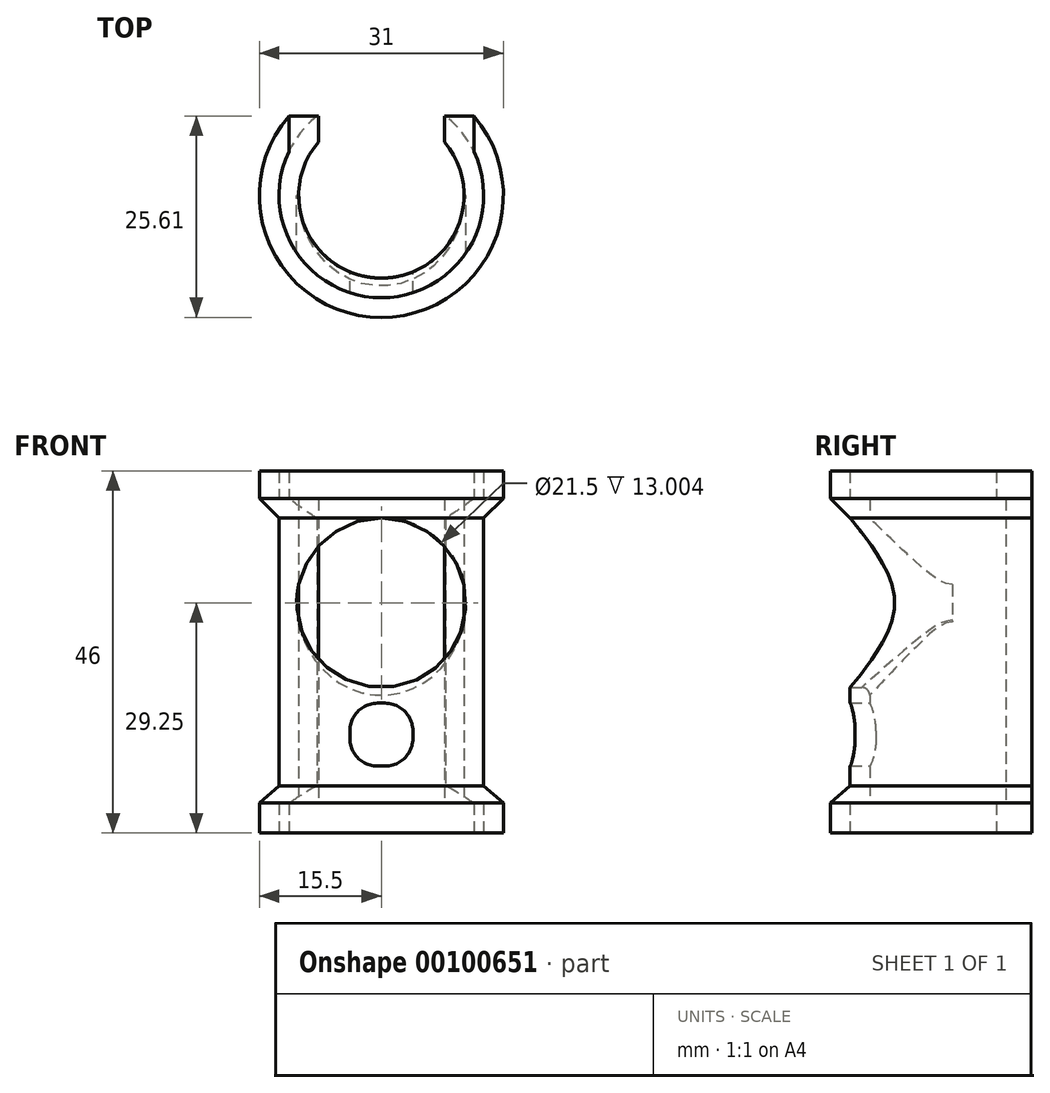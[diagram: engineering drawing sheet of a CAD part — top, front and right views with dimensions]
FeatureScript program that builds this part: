
annotation { "Feature Type Name" : "Feature", "Feature Type Description" : "" }
export const myFeature = defineFeature(function(context is Context, id is Id, definition is map)
    precondition{}
    {
        {
            var Q0;
            Q0=qCreatedBy(makeId("Front.planeOp"),FACE);
            var sketch = newSketch(context, id + "F0", { "sketchPlane" : qUnion([Q0])});
            skLineSegment(sketch, "E0", {"start": v(-13, 0) * mm, "end": v(-13, 3.8) * mm});
            skLineSegment(sketch, "E1", {"start": v(-13, 3.8) * mm, "end": v(-10.5, 3.8) * mm});
            skLineSegment(sketch, "E2", {"start": v(-10.5, 3.8) * mm, "end": v(-10.5, 42.5) * mm});
            skLineSegment(sketch, "E3", {"start": v(-13, 42.5) * mm, "end": v(-13, 46) * mm});
            skLineSegment(sketch, "E4", {"start": v(-13, 42.5) * mm, "end": v(-10.5, 42.5) * mm});
            skLineSegment(sketch, "E5", {"start": v(-13, 46) * mm, "end": v(-15.5, 46) * mm});
            skLineSegment(sketch, "E6", {"start": v(-15.5, 46) * mm, "end": v(-15.5, 42.5) * mm});
            skLineSegment(sketch, "E7", {"start": v(-13, 40) * mm, "end": v(-13, 6) * mm});
            skLineSegment(sketch, "E8", {"start": v(-15.5, 3.8) * mm, "end": v(-15.5, 0) * mm});
            skLineSegment(sketch, "E9", {"start": v(-15.5, 0) * mm, "end": v(-13, 0) * mm});
            skLineSegment(sketch, "E10", {"start": v(0, 0) * mm, "end": v(0, 49.8) * mm, "construction": true});
            skLineSegment(sketch, "E11", {"start": v(-15.5, 42.5) * mm, "end": v(-13, 40) * mm});
            skLineSegment(sketch, "E12", {"start": v(-15.5, 3.8) * mm, "end": v(-13, 6) * mm});
            skPoint(sketch, "E13.orphan", {"position": v(-13, 41) * mm});
            skPoint(sketch, "E14.orphan", {"position": v(-13, 3.5) * mm});
            skSolve(sketch);
        }
        {
            var Q0;
            Q0 = qSketchRegion(id + "F0", true);
            var Q1;
            Q1=sQuery(id+"F0.wireOp",EDGE,"E10");
            revolve(context, id + "F1", {"entities" : qUnion([Q0]), "axis" : qUnion([Q1]), "revolveType" : RevolveType.FULL});
        }
        {
            var Q0;
            Q0=makeQuery(id+"F1.opRevolve","SWEPT_FACE",FACE,{"disambiguationData":[OSD([sQuery(id+"F0.wireOp",EDGE,"E5")])]});
            var sketch = newSketch(context, id + "F2", { "sketchPlane" : qUnion([Q0])});
            skLineSegment(sketch, "E15.bottom", {"start": v(-8, 18.1) * mm, "end": v(8, 18.1) * mm});
            skLineSegment(sketch, "E15.top", {"start": v(-8, 5.31) * mm, "end": v(8, 5.31) * mm});
            skLineSegment(sketch, "E15.left", {"start": v(-8, 18.1) * mm, "end": v(-8, 5.31) * mm});
            skLineSegment(sketch, "E15.right", {"start": v(8, 18.1) * mm, "end": v(8, 5.31) * mm});
            skSolve(sketch);
        }
        {
            var Q0;
            Q0 = qSketchRegion(id + "F2", true);
            extrude(context, id + "F3", {"entities" : qUnion([Q0]), "operationType" : NewBodyOperationType.REMOVE, "endBound" : BoundingType.THROUGH_ALL, "oppositeDirection" : true, "depth" : 25 * mm});
        }
        {
            var Q0;
            Q0=makeQuery(id+"F1.opRevolve","SWEPT_FACE",FACE,{"disambiguationData":[OSD([sQuery(id+"F0.wireOp",EDGE,"E5")])]});
            var sketch = newSketch(context, id + "F4", { "sketchPlane" : qUnion([Q0])});
            skLineSegment(sketch, "E16.bottom", {"start": v(-11.75, 4.07) * mm, "end": v(11.75, 4.07) * mm});
            skLineSegment(sketch, "E16.top", {"start": v(-11.75, 17.53) * mm, "end": v(11.75, 17.53) * mm});
            skLineSegment(sketch, "E16.left", {"start": v(-11.75, 4.07) * mm, "end": v(-11.75, 17.53) * mm});
            skLineSegment(sketch, "E16.right", {"start": v(11.75, 4.07) * mm, "end": v(11.75, 17.53) * mm});
            skSolve(sketch);
        }
        {
            var Q0;
            Q0 = qSketchRegion(id + "F4", true);
            var Q1;
            Q1=makeQuery(id+"F1.opRevolve","SWEPT_FACE",FACE,{"disambiguationData":[OSD([sQuery(id+"F0.wireOp",EDGE,"E4")])]});
            extrude(context, id + "F5", {"entities" : qUnion([Q0]), "operationType" : NewBodyOperationType.REMOVE, "endBound" : BoundingType.UP_TO_SURFACE, "oppositeDirection" : true, "endBoundEntityFace" : qUnion([Q1]), "depth" : 25 * mm});
        }
        {
            var Q0;
            Q0=makeQuery(id+"F1.opRevolve","SWEPT_FACE",FACE,{"disambiguationData":[OSD([sQuery(id+"F0.wireOp",EDGE,"E9")])]});
            var sketch = newSketch(context, id + "F6", { "sketchPlane" : qUnion([Q0])});
            skLineSegment(sketch, "E17.bottom", {"start": v(-11.75, -15.87) * mm, "end": v(11.75, -15.87) * mm});
            skLineSegment(sketch, "E17.top", {"start": v(-11.75, -2.84) * mm, "end": v(11.75, -2.84) * mm});
            skLineSegment(sketch, "E17.left", {"start": v(-11.75, -15.87) * mm, "end": v(-11.75, -2.84) * mm});
            skLineSegment(sketch, "E17.right", {"start": v(11.75, -15.87) * mm, "end": v(11.75, -2.84) * mm});
            skSolve(sketch);
        }
        {
            var Q0;
            Q0 = qSketchRegion(id + "F6", true);
            var Q1;
            Q1=makeQuery(id+"F1.opRevolve","SWEPT_FACE",FACE,{"disambiguationData":[OSD([sQuery(id+"F0.wireOp",EDGE,"E1")])]});
            extrude(context, id + "F7", {"entities" : qUnion([Q0]), "operationType" : NewBodyOperationType.REMOVE, "endBound" : BoundingType.UP_TO_SURFACE, "oppositeDirection" : true, "endBoundEntityFace" : qUnion([Q1]), "depth" : 25 * mm});
        }
        {
            var Q0;
            Q0=qCreatedBy(makeId("Front.planeOp"),FACE);
            var sketch = newSketch(context, id + "F8", { "sketchPlane" : qUnion([Q0])});
            skCircle(sketch, "E18", {"center": v(0, 29.25) * mm, "radius": 10.75 * mm});
            skSolve(sketch);
        }
        {
            var Q0;
            Q0=makeQuery(id+"F8.imprint","IMPRINT",FACE,{"disambiguationData":[TD([[makeQuery(id+"F8.imprint","IMPRINT",EDGE,{"derivedFrom":sQuery(id+"F8.wireOp",EDGE,"E18")}),1.0]])]});
            extrude(context, id + "F9", {"entities" : qUnion([Q0]), "operationType" : NewBodyOperationType.REMOVE, "depth" : 25 * mm});
        }
        {
            var Q0;
            Q0=qCreatedBy(makeId("Right.planeOp"),FACE);
            var sketch = newSketch(context, id + "F10", { "sketchPlane" : qUnion([Q0])});
            skLineSegment(sketch, "E19.bottom", {"start": v(2, 37) * mm, "end": v(2, 37) * mm});
            skLineSegment(sketch, "E19.top", {"start": v(2, 12) * mm, "end": v(2, 12) * mm});
            skLineSegment(sketch, "E19.left", {"start": v(-1.5, 33.5) * mm, "end": v(-1.5, 15.5) * mm});
            skLineSegment(sketch, "E19.right", {"start": v(5.5, 33.5) * mm, "end": v(5.5, 15.5) * mm});
            skPoint(sketch, "E20.visualSharp", {"position": v(5.5, 37) * mm});
            skArc(sketch, "E20.filletArc", {"start": v(5.5, 33.5) * mm, "mid": v(4.47, 35.97) * mm, "end": v(2, 37) * mm});
            skPoint(sketch, "E21.visualSharp", {"position": v(5.5, 12) * mm});
            skArc(sketch, "E21.filletArc", {"start": v(2, 12) * mm, "mid": v(4.47, 13.03) * mm, "end": v(5.5, 15.5) * mm});
            skPoint(sketch, "E22.visualSharp", {"position": v(-1.5, 12) * mm});
            skArc(sketch, "E22.filletArc", {"start": v(-1.5, 15.5) * mm, "mid": v(-0.47, 13.03) * mm, "end": v(2, 12) * mm});
            skPoint(sketch, "E23.visualSharp", {"position": v(-1.5, 37) * mm});
            skArc(sketch, "E23.filletArc", {"start": v(2, 37) * mm, "mid": v(-0.47, 35.97) * mm, "end": v(-1.5, 33.5) * mm});
            skSolve(sketch);
        }
        {
            var Q0;
            Q0=qCreatedBy(makeId("Top.planeOp"),FACE);
            var sketch = newSketch(context, id + "F11", { "sketchPlane" : qUnion([Q0])});
            skLineSegment(sketch, "E24.bottom", {"start": v(-15.82, 20.1) * mm, "end": v(15.95, 20.1) * mm});
            skLineSegment(sketch, "E24.top", {"start": v(-15.82, 10.1) * mm, "end": v(15.95, 10.1) * mm});
            skLineSegment(sketch, "E24.left", {"start": v(-15.82, 20.1) * mm, "end": v(-15.82, 10.1) * mm});
            skLineSegment(sketch, "E24.right", {"start": v(15.95, 20.1) * mm, "end": v(15.95, 10.1) * mm});
            skSolve(sketch);
        }
        {
            var Q0;
            Q0=makeQuery(id+"F11.imprint","IMPRINT",FACE,{"disambiguationData":[TD([[makeQuery(id+"F11.imprint","IMPRINT",EDGE,{"derivedFrom":sQuery(id+"F11.wireOp",EDGE,"E24.bottom")}),-1.0]])]});
            extrude(context, id + "F12", {"entities" : qUnion([Q0]), "operationType" : NewBodyOperationType.REMOVE, "endBound" : BoundingType.THROUGH_ALL, "depth" : 25 * mm});
        }
        {
            var Q0;
            Q0=qCreatedBy(makeId("Front.planeOp"),FACE);
            var sketch = newSketch(context, id + "F13", { "sketchPlane" : qUnion([Q0])});
            skLineSegment(sketch, "E25.bottom", {"start": v(-0.5, 16.5) * mm, "end": v(0.5, 16.5) * mm});
            skLineSegment(sketch, "E25.top", {"start": v(-0.5, 8.5) * mm, "end": v(0.5, 8.5) * mm});
            skLineSegment(sketch, "E25.left", {"start": v(-4, 13) * mm, "end": v(-4, 12) * mm});
            skLineSegment(sketch, "E25.right", {"start": v(4, 13) * mm, "end": v(4, 12) * mm});
            skPoint(sketch, "E26.visualSharp", {"position": v(-4, 16.5) * mm});
            skArc(sketch, "E26.filletArc", {"start": v(-0.5, 16.5) * mm, "mid": v(-2.97, 15.47) * mm, "end": v(-4, 13) * mm});
            skPoint(sketch, "E27.visualSharp", {"position": v(4, 16.5) * mm});
            skArc(sketch, "E27.filletArc", {"start": v(4, 13) * mm, "mid": v(2.97, 15.47) * mm, "end": v(0.5, 16.5) * mm});
            skPoint(sketch, "E28.visualSharp", {"position": v(-4, 8.5) * mm});
            skArc(sketch, "E28.filletArc", {"start": v(-4, 12) * mm, "mid": v(-2.97, 9.53) * mm, "end": v(-0.5, 8.5) * mm});
            skPoint(sketch, "E29.visualSharp", {"position": v(4, 8.5) * mm});
            skArc(sketch, "E29.filletArc", {"start": v(0.5, 8.5) * mm, "mid": v(2.97, 9.53) * mm, "end": v(4, 12) * mm});
            skSolve(sketch);
        }
        {
            var Q0;
            Q0 = qSketchRegion(id + "F13", true);
            extrude(context, id + "F14", {"entities" : qUnion([Q0]), "operationType" : NewBodyOperationType.REMOVE, "depth" : 25 * mm});
        }
        {
            var Q0;
            Q0=makeQuery(id+"F9.boolean.opBoolean","INTERSECT",EDGE,{"disambiguationData":[OD(0.0)],"derivedFrom":[makeQuery(id+"F1.opRevolve","SWEPT_FACE",FACE,{"disambiguationData":[OSD([sQuery(id+"F0.wireOp",EDGE,"E2")])]}),makeQuery(id+"F9.opExtrude","SWEPT_FACE",FACE,{"disambiguationData":[OSD([sQuery(id+"F8.wireOp",EDGE,"E18")])]})]});
            fillet(context, id + "F15", {"entities" : qUnion([Q0]), "radius" : 1 * mm, "tangentPropagation" : true, "allowEdgeOverflow" : false});
        }
    });
